# Revit family: Toilet-Chair_Height-American_Standard-Estate-240AA704.020_Series
name_source: partatom
category: Plumbing Fixtures
units: mm (PartAtom-declared; Revit-internal decimal feet)

## family parameters
Always vertical = No
Cut with Voids When Loaded = No
OmniClass Number = 23.45.05.21.11.11
OmniClass Title = Water Operated Water Closets
Part Type = Normal
Room Calculation Point = No
Round Connector Dimension = Use Diameter
Shared = Yes
Work Plane-Based = Yes

## types (3) — shared parameters
3193A.100 Chair Height Elongated Bowl with Seat = No
4000.704 Tank = No
5024A.65G Slow-Close Seat Packed with Bowl = No
ADA Compliant = Yes
Assembly Code = D2010110
Bowl Shape = Elongated
CEC Compliant = Yes
CW Connection = Yes
CWFU = 10
CalGreen Compliant = Yes
Cold Water Connection Diameter = 1/2"
Cold Water Connection Height = 10"
Cold Water Connection Width = 6"
Compliance Certifications = Meets or Exceeds the Following Specifications • ASME A112.19.2/CSA B45.1 for Vitreous China Fixtures • US EPA WaterSense® Specification for HETs
Default Elevation = 16 1/2"
Description = Estate® Skirted Two-Piece 1.28 gpf/4.8 Lpf Chair Height Elongated Toilet With Seat
Finish = Vitreous China-American Standard-020-White
Flush Rate = 4.8 Lpf/1.28 gpf
HW Connection = No
Height = 30 11/16"
Inlet Position Constraint = 2 1/4"
Installation Type = Floor Mounted
Length = 30 1/4"
Manufacturer = American Standard
Material = Vitreous China-American Standard-020-White
Model = 240AA704.020 with 7381458-300.0020A
Product Documentation Link = https://americanstandard.box.com
Product Page URL = https://www.americanstandard-us.com
Supply Inlet Position 1 (2 1/4") = Yes
Supply Inlet Position 2 (8") = No
URL = http://www.americanstandard-us.com
Vent Connection = No
WFU = 10
Warranty Information = Lifetime warranty on chinaware, 5 year warranty on all mechanical parts, and 1 year warranty
on seat
Waste Connection = Yes
Waste Connection Diameter = 2 1/8"
Width = 15 13/16"
zero-valued in all types: HWFU

## per-type parameters (varying)
| type | 7381458-300.0020A Estate Left Hand Trip Lever CHROME | 7381458-300.0130A Estate Left Hand Trip Lever POLISHED NICKEL | 7381458-300.2430A Estate Left Hand Trip Lever MATTE BLACK | Trip Lever Material |
| 240AA704.020 with 7381458-300.0020A | Yes | No | No | Metal-American Standard-002-Polished Chrome |
| 240AA704.020 with 7381458-300.0130A | No | Yes | No | Brass-American Standard-013-Polished Nickel |
| 240AA704.020 with 7381458-300.2430A | No | No | Yes | Brass-American Standard-243-Matte Black |

## geometry (parser evidence)
native form markers: Sweep x2
no freeform markers — native parametric forms only
